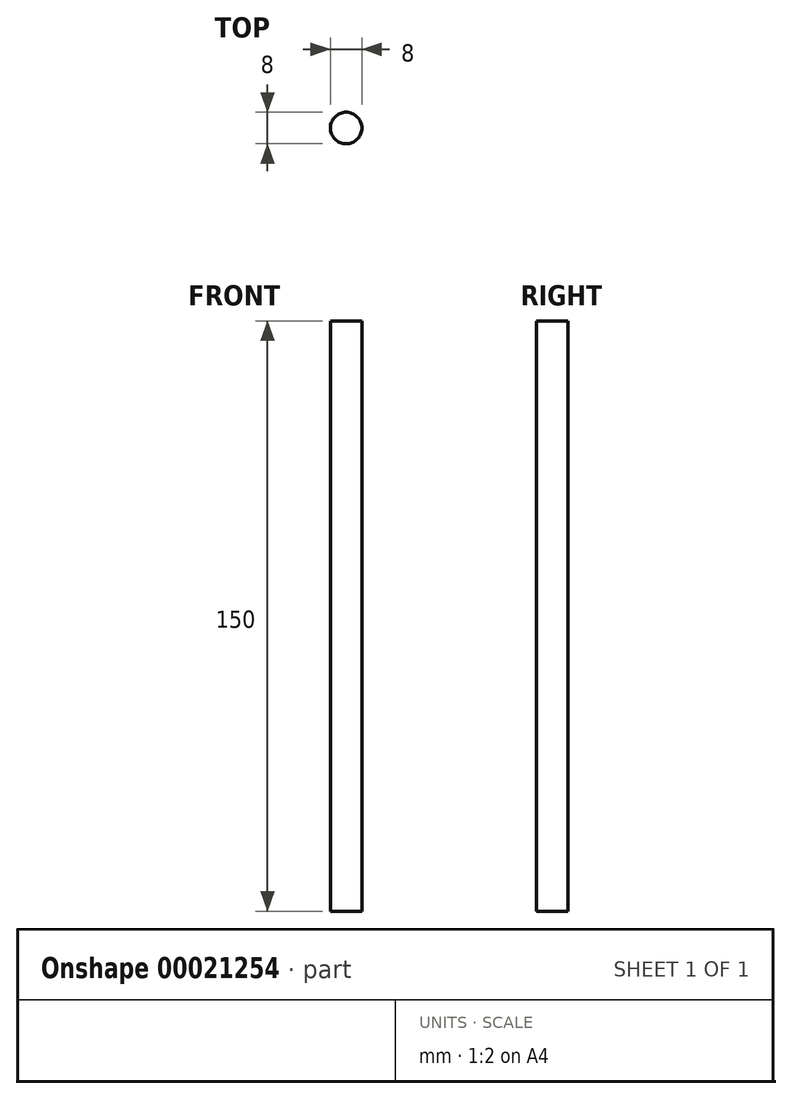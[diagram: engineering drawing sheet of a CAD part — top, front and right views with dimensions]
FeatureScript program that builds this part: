
annotation { "Feature Type Name" : "Feature", "Feature Type Description" : "" }
export const myFeature = defineFeature(function(context is Context, id is Id, definition is map)
    precondition{}
    {
        {
            var Q0;
            Q0=qCreatedBy(makeId("Top.planeOp"),FACE);
            var sketch = newSketch(context, id + "F0", { "sketchPlane" : qUnion([Q0])});
            skCircle(sketch, "E0", {"center": v(0, 0) * mm, "radius": 4 * mm});
            skSolve(sketch);
        }
        {
            var Q0;
            Q0=qSketchRegion(id+"F0",true);
            extrude(context, id + "F1", {"entities" : qUnion([Q0]), "depth" : 150 * mm});
        }
    });
